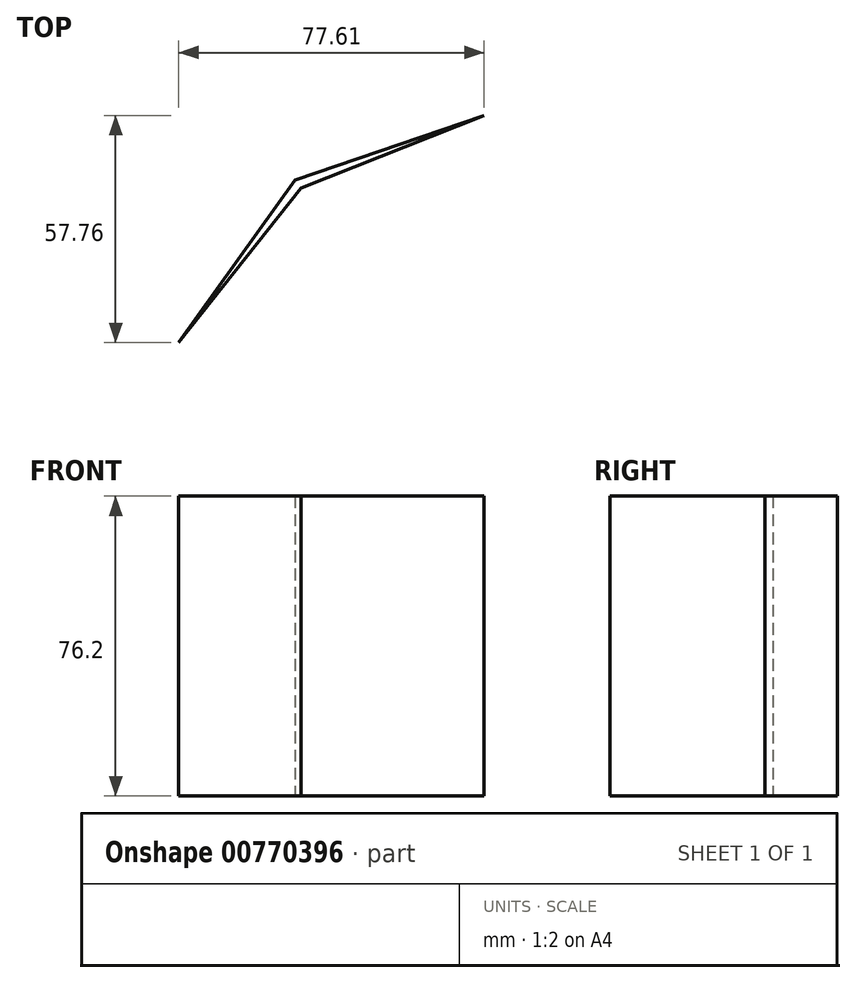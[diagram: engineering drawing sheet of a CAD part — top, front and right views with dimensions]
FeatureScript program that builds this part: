
annotation { "Feature Type Name" : "Feature", "Feature Type Description" : "" }
export const myFeature = defineFeature(function(context is Context, id is Id, definition is map)
    precondition{}
    {
        {
            var Q0;
            Q0=qCreatedBy(makeId("Top.planeOp"),FACE);
            var sketch = newSketch(context, id + "F0", { "sketchPlane" : qUnion([Q0])});
            skLineSegment(sketch, "E0", {"start": v(-29.55, -15.76) * mm, "end": v(1.55, 23.54) * mm});
            skLineSegment(sketch, "E1", {"start": v(1.55, 23.54) * mm, "end": v(48.06, 42) * mm});
            skLineSegment(sketch, "E2", {"start": v(-29.55, -15.76) * mm, "end": v(0, 25.56) * mm});
            skLineSegment(sketch, "E3", {"start": v(0, 25.56) * mm, "end": v(48.06, 42) * mm});
            skSolve(sketch);
        }
        {
            var Q0;
            Q0 = qSketchRegion(id + "F0", true);
            extrude(context, id + "F1", {"entities" : qUnion([Q0]), "depth" : 76.2 * mm, "offsetDistance" : 25.4 * mm});
        }
    });
